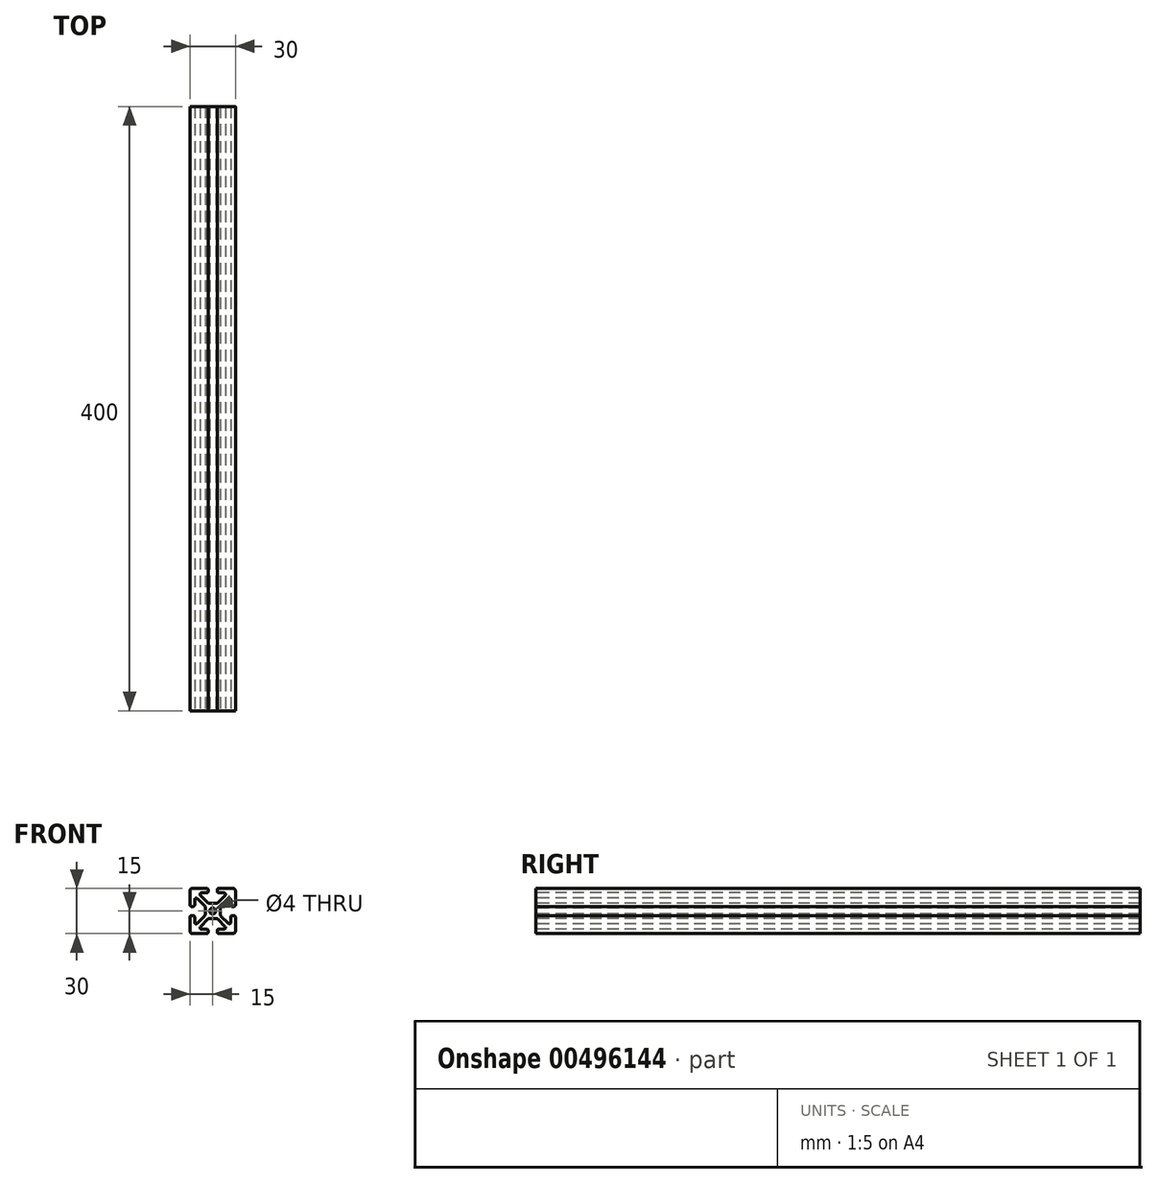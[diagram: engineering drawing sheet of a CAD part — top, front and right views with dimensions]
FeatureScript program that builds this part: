
annotation { "Feature Type Name" : "Feature", "Feature Type Description" : "" }
export const myFeature = defineFeature(function(context is Context, id is Id, definition is map)
    precondition{}
    {
        {
            var Q0;
            Q0=qCreatedBy(makeId("Front.planeOp"),FACE);
            var sketch = newSketch(context, id + "F0", { "sketchPlane" : qUnion([Q0])});
            skLineSegment(sketch, "E0.bottom", {"start": v(13.5, 15) * mm, "end": v(4, 15) * mm});
            skLineSegment(sketch, "E0.top", {"start": v(13.5, -15) * mm, "end": v(4, -15) * mm});
            skLineSegment(sketch, "E0.left", {"start": v(15, 13.5) * mm, "end": v(15, 4) * mm});
            skLineSegment(sketch, "E0.right", {"start": v(-15, 13.5) * mm, "end": v(-15, 4) * mm});
            skPoint(sketch, "E0.middle", {"position": v(0, 0) * mm});
            skLineSegment(sketch, "E1.bottom", {"start": v(7.46, 12) * mm, "end": v(4, 12) * mm});
            skLineSegment(sketch, "E1.top", {"start": v(7.46, -12) * mm, "end": v(4, -12) * mm});
            skLineSegment(sketch, "E1.left", {"start": v(12, 7.46) * mm, "end": v(12, 4) * mm});
            skLineSegment(sketch, "E1.right", {"start": v(-12, 7.46) * mm, "end": v(-12, 4) * mm});
            skLineSegment(sketch, "E2", {"start": v(8.17, 10.3) * mm, "end": v(3.32, 5.44) * mm});
            skLineSegment(sketch, "E3", {"start": v(-8.17, -10.3) * mm, "end": v(-3.32, -5.44) * mm});
            skLineSegment(sketch, "E4", {"start": v(-8.17, 10.3) * mm, "end": v(-3.32, 5.44) * mm});
            skLineSegment(sketch, "E5", {"start": v(-10.3, 8.17) * mm, "end": v(-5, 2.88) * mm});
            skPoint(sketch, "E6.orphan", {"position": v(12, 12) * mm});
            skPoint(sketch, "E7.orphan", {"position": v(12, -12) * mm});
            skPoint(sketch, "E8.orphan", {"position": v(-12, -12) * mm});
            skPoint(sketch, "E9.orphan", {"position": v(-12, 12) * mm});
            skLineSegment(sketch, "E10.trimOffspring", {"start": v(-5.44, -3.32) * mm, "end": v(-10.3, -8.17) * mm});
            skLineSegment(sketch, "E11.trimOffspring", {"start": v(5.44, -3.32) * mm, "end": v(10.3, -8.17) * mm});
            skLineSegment(sketch, "E12.trimOffspring", {"start": v(5.44, 3.32) * mm, "end": v(10.3, 8.17) * mm});
            skLineSegment(sketch, "E13.trimOffspring", {"start": v(3.32, -5.44) * mm, "end": v(8.17, -10.3) * mm});
            skLineSegment(sketch, "E14.bottom", {"start": v(2.26, 5) * mm, "end": v(-2.26, 5) * mm});
            skLineSegment(sketch, "E14.top", {"start": v(2.26, -5) * mm, "end": v(-2.26, -5) * mm});
            skLineSegment(sketch, "E14.left", {"start": v(5, 2.26) * mm, "end": v(5, -2.26) * mm});
            skLineSegment(sketch, "E14.right", {"start": v(-5, 2.88) * mm, "end": v(-5, -2.26) * mm});
            skPoint(sketch, "E15.orphan", {"position": v(5, 5) * mm});
            skPoint(sketch, "E16.orphan", {"position": v(5, -5) * mm});
            skPoint(sketch, "E17.orphan", {"position": v(-5, -5) * mm});
            skPoint(sketch, "E18.orphan", {"position": v(-5, 5) * mm});
            skCircle(sketch, "E19", {"center": v(0, 0) * mm, "radius": 2 * mm});
            skLineSegment(sketch, "E20", {"start": v(-3, 14) * mm, "end": v(-3, 13) * mm});
            skLineSegment(sketch, "E21", {"start": v(3, 14) * mm, "end": v(3, 13) * mm});
            skLineSegment(sketch, "E22.trimOffspring", {"start": v(-3, -13) * mm, "end": v(-3, -14) * mm});
            skLineSegment(sketch, "E23.trimOffspring", {"start": v(-4, 12) * mm, "end": v(-7.46, 12) * mm});
            skLineSegment(sketch, "E24.trimOffspring", {"start": v(-4, 15) * mm, "end": v(-13.5, 15) * mm});
            skLineSegment(sketch, "E25.trimOffspring", {"start": v(3, -13) * mm, "end": v(3, -14) * mm});
            skLineSegment(sketch, "E26.trimOffspring", {"start": v(-4, -12) * mm, "end": v(-7.46, -12) * mm});
            skLineSegment(sketch, "E27.trimOffspring", {"start": v(-4, -15) * mm, "end": v(-13.5, -15) * mm});
            skLineSegment(sketch, "E28", {"start": v(-14, 3) * mm, "end": v(-13, 3) * mm});
            skLineSegment(sketch, "E29", {"start": v(-14, -3) * mm, "end": v(-13, -3) * mm});
            skLineSegment(sketch, "E30.trimOffspring", {"start": v(-12, -4) * mm, "end": v(-12, -7.46) * mm});
            skLineSegment(sketch, "E31.trimOffspring", {"start": v(-15, -4) * mm, "end": v(-15, -13.5) * mm});
            skLineSegment(sketch, "E32.trimOffspring", {"start": v(13, 3) * mm, "end": v(14, 3) * mm});
            skLineSegment(sketch, "E33.trimOffspring", {"start": v(13, -3) * mm, "end": v(14, -3) * mm});
            skLineSegment(sketch, "E34.trimOffspring", {"start": v(12, -4) * mm, "end": v(12, -7.46) * mm});
            skLineSegment(sketch, "E35.trimOffspring", {"start": v(15, -4) * mm, "end": v(15, -13.5) * mm});
            skPoint(sketch, "E36.visualSharp", {"position": v(-15, 15) * mm});
            skArc(sketch, "E36.filletArc", {"start": v(-13.5, 15) * mm, "mid": v(-14.56, 14.56) * mm, "end": v(-15, 13.5) * mm});
            skPoint(sketch, "E37.visualSharp", {"position": v(15, 15) * mm});
            skArc(sketch, "E37.filletArc", {"start": v(15, 13.5) * mm, "mid": v(14.56, 14.56) * mm, "end": v(13.5, 15) * mm});
            skPoint(sketch, "E38.visualSharp", {"position": v(15, -15) * mm});
            skArc(sketch, "E38.filletArc", {"start": v(13.5, -15) * mm, "mid": v(14.56, -14.56) * mm, "end": v(15, -13.5) * mm});
            skPoint(sketch, "E39.visualSharp", {"position": v(-15, -15) * mm});
            skArc(sketch, "E39.filletArc", {"start": v(-15, -13.5) * mm, "mid": v(-14.56, -14.56) * mm, "end": v(-13.5, -15) * mm});
            skPoint(sketch, "E40.visualSharp", {"position": v(-5, -2.88) * mm});
            skArc(sketch, "E40.filletArc", {"start": v(-5.44, -3.32) * mm, "mid": v(-5.11, -2.83) * mm, "end": v(-5, -2.26) * mm});
            skPoint(sketch, "E41.visualSharp", {"position": v(-2.88, -5) * mm});
            skArc(sketch, "E41.filletArc", {"start": v(-2.26, -5) * mm, "mid": v(-2.83, -5.11) * mm, "end": v(-3.32, -5.44) * mm});
            skPoint(sketch, "E42.visualSharp", {"position": v(2.88, -5) * mm});
            skArc(sketch, "E42.filletArc", {"start": v(3.32, -5.44) * mm, "mid": v(2.83, -5.11) * mm, "end": v(2.26, -5) * mm});
            skPoint(sketch, "E43.visualSharp", {"position": v(5, -2.88) * mm});
            skArc(sketch, "E43.filletArc", {"start": v(5, -2.26) * mm, "mid": v(5.11, -2.83) * mm, "end": v(5.44, -3.32) * mm});
            skPoint(sketch, "E44.visualSharp", {"position": v(5, 2.88) * mm});
            skArc(sketch, "E44.filletArc", {"start": v(5.44, 3.32) * mm, "mid": v(5.11, 2.83) * mm, "end": v(5, 2.26) * mm});
            skPoint(sketch, "E45.visualSharp", {"position": v(2.88, 5) * mm});
            skArc(sketch, "E45.filletArc", {"start": v(2.26, 5) * mm, "mid": v(2.83, 5.11) * mm, "end": v(3.32, 5.44) * mm});
            skPoint(sketch, "E46.visualSharp", {"position": v(-2.88, 5) * mm});
            skArc(sketch, "E46.filletArc", {"start": v(-3.32, 5.44) * mm, "mid": v(-2.83, 5.11) * mm, "end": v(-2.26, 5) * mm});
            skPoint(sketch, "E47.visualSharp", {"position": v(-3, 12) * mm});
            skArc(sketch, "E47.filletArc", {"start": v(-4, 12) * mm, "mid": v(-3.3, 12.3) * mm, "end": v(-3, 13) * mm});
            skPoint(sketch, "E48.visualSharp", {"position": v(-3, 15) * mm});
            skArc(sketch, "E48.filletArc", {"start": v(-3, 14) * mm, "mid": v(-3.3, 14.7) * mm, "end": v(-4, 15) * mm});
            skPoint(sketch, "E49.visualSharp", {"position": v(3, 15) * mm});
            skArc(sketch, "E49.filletArc", {"start": v(4, 15) * mm, "mid": v(3.3, 14.7) * mm, "end": v(3, 14) * mm});
            skPoint(sketch, "E50.visualSharp", {"position": v(3, 12) * mm});
            skArc(sketch, "E50.filletArc", {"start": v(3, 13) * mm, "mid": v(3.3, 12.3) * mm, "end": v(4, 12) * mm});
            skPoint(sketch, "E51.visualSharp", {"position": v(12, 3) * mm});
            skArc(sketch, "E51.filletArc", {"start": v(12, 4) * mm, "mid": v(12.3, 3.3) * mm, "end": v(13, 3) * mm});
            skPoint(sketch, "E52.visualSharp", {"position": v(15, 3) * mm});
            skArc(sketch, "E52.filletArc", {"start": v(14, 3) * mm, "mid": v(14.7, 3.3) * mm, "end": v(15, 4) * mm});
            skPoint(sketch, "E53.visualSharp", {"position": v(15, -3) * mm});
            skArc(sketch, "E53.filletArc", {"start": v(15, -4) * mm, "mid": v(14.7, -3.3) * mm, "end": v(14, -3) * mm});
            skPoint(sketch, "E54.visualSharp", {"position": v(12, -3) * mm});
            skArc(sketch, "E54.filletArc", {"start": v(13, -3) * mm, "mid": v(12.3, -3.3) * mm, "end": v(12, -4) * mm});
            skPoint(sketch, "E55.visualSharp", {"position": v(3, -12) * mm});
            skArc(sketch, "E55.filletArc", {"start": v(4, -12) * mm, "mid": v(3.3, -12.3) * mm, "end": v(3, -13) * mm});
            skPoint(sketch, "E56.visualSharp", {"position": v(3, -15) * mm});
            skArc(sketch, "E56.filletArc", {"start": v(3, -14) * mm, "mid": v(3.3, -14.7) * mm, "end": v(4, -15) * mm});
            skPoint(sketch, "E57.visualSharp", {"position": v(-3, -12) * mm});
            skArc(sketch, "E57.filletArc", {"start": v(-3, -13) * mm, "mid": v(-3.3, -12.3) * mm, "end": v(-4, -12) * mm});
            skPoint(sketch, "E58.visualSharp", {"position": v(-3, -15) * mm});
            skArc(sketch, "E58.filletArc", {"start": v(-4, -15) * mm, "mid": v(-3.3, -14.7) * mm, "end": v(-3, -14) * mm});
            skPoint(sketch, "E59.visualSharp", {"position": v(-12, -3) * mm});
            skArc(sketch, "E59.filletArc", {"start": v(-12, -4) * mm, "mid": v(-12.3, -3.3) * mm, "end": v(-13, -3) * mm});
            skPoint(sketch, "E60.visualSharp", {"position": v(-15, -3) * mm});
            skArc(sketch, "E60.filletArc", {"start": v(-14, -3) * mm, "mid": v(-14.7, -3.3) * mm, "end": v(-15, -4) * mm});
            skPoint(sketch, "E61.visualSharp", {"position": v(-15, 3) * mm});
            skArc(sketch, "E61.filletArc", {"start": v(-15, 4) * mm, "mid": v(-14.7, 3.3) * mm, "end": v(-14, 3) * mm});
            skPoint(sketch, "E62.visualSharp", {"position": v(-12, 3) * mm});
            skArc(sketch, "E62.filletArc", {"start": v(-13, 3) * mm, "mid": v(-12.3, 3.3) * mm, "end": v(-12, 4) * mm});
            skPoint(sketch, "E63.visualSharp", {"position": v(9.88, 12) * mm});
            skArc(sketch, "E63.filletArc", {"start": v(8.17, 10.3) * mm, "mid": v(8.39, 11.38) * mm, "end": v(7.46, 12) * mm});
            skPoint(sketch, "E64.visualSharp", {"position": v(12, 9.88) * mm});
            skArc(sketch, "E64.filletArc", {"start": v(12, 7.46) * mm, "mid": v(11.38, 8.39) * mm, "end": v(10.3, 8.17) * mm});
            skPoint(sketch, "E65.visualSharp", {"position": v(12, -9.88) * mm});
            skArc(sketch, "E65.filletArc", {"start": v(10.3, -8.17) * mm, "mid": v(11.38, -8.39) * mm, "end": v(12, -7.46) * mm});
            skPoint(sketch, "E66.visualSharp", {"position": v(9.88, -12) * mm});
            skArc(sketch, "E66.filletArc", {"start": v(7.46, -12) * mm, "mid": v(8.39, -11.38) * mm, "end": v(8.17, -10.3) * mm});
            skPoint(sketch, "E67.visualSharp", {"position": v(-12, -9.88) * mm});
            skArc(sketch, "E67.filletArc", {"start": v(-12, -7.46) * mm, "mid": v(-11.38, -8.39) * mm, "end": v(-10.3, -8.17) * mm});
            skPoint(sketch, "E68.visualSharp", {"position": v(-9.88, -12) * mm});
            skArc(sketch, "E68.filletArc", {"start": v(-8.17, -10.3) * mm, "mid": v(-8.39, -11.38) * mm, "end": v(-7.46, -12) * mm});
            skPoint(sketch, "E69.visualSharp", {"position": v(-12, 9.88) * mm});
            skArc(sketch, "E69.filletArc", {"start": v(-10.3, 8.17) * mm, "mid": v(-11.38, 8.39) * mm, "end": v(-12, 7.46) * mm});
            skPoint(sketch, "E70.visualSharp", {"position": v(-9.88, 12) * mm});
            skArc(sketch, "E70.filletArc", {"start": v(-7.46, 12) * mm, "mid": v(-8.39, 11.38) * mm, "end": v(-8.17, 10.3) * mm});
            skSolve(sketch);
        }
        {
            var Q0;
            Q0=qSketchRegion(id+"F0",true);
            extrude(context, id + "F1", {"entities" : qUnion([Q0]), "oppositeDirection" : true, "depth" : 400 * mm, "offsetDistance" : 25 * mm});
        }
    });
